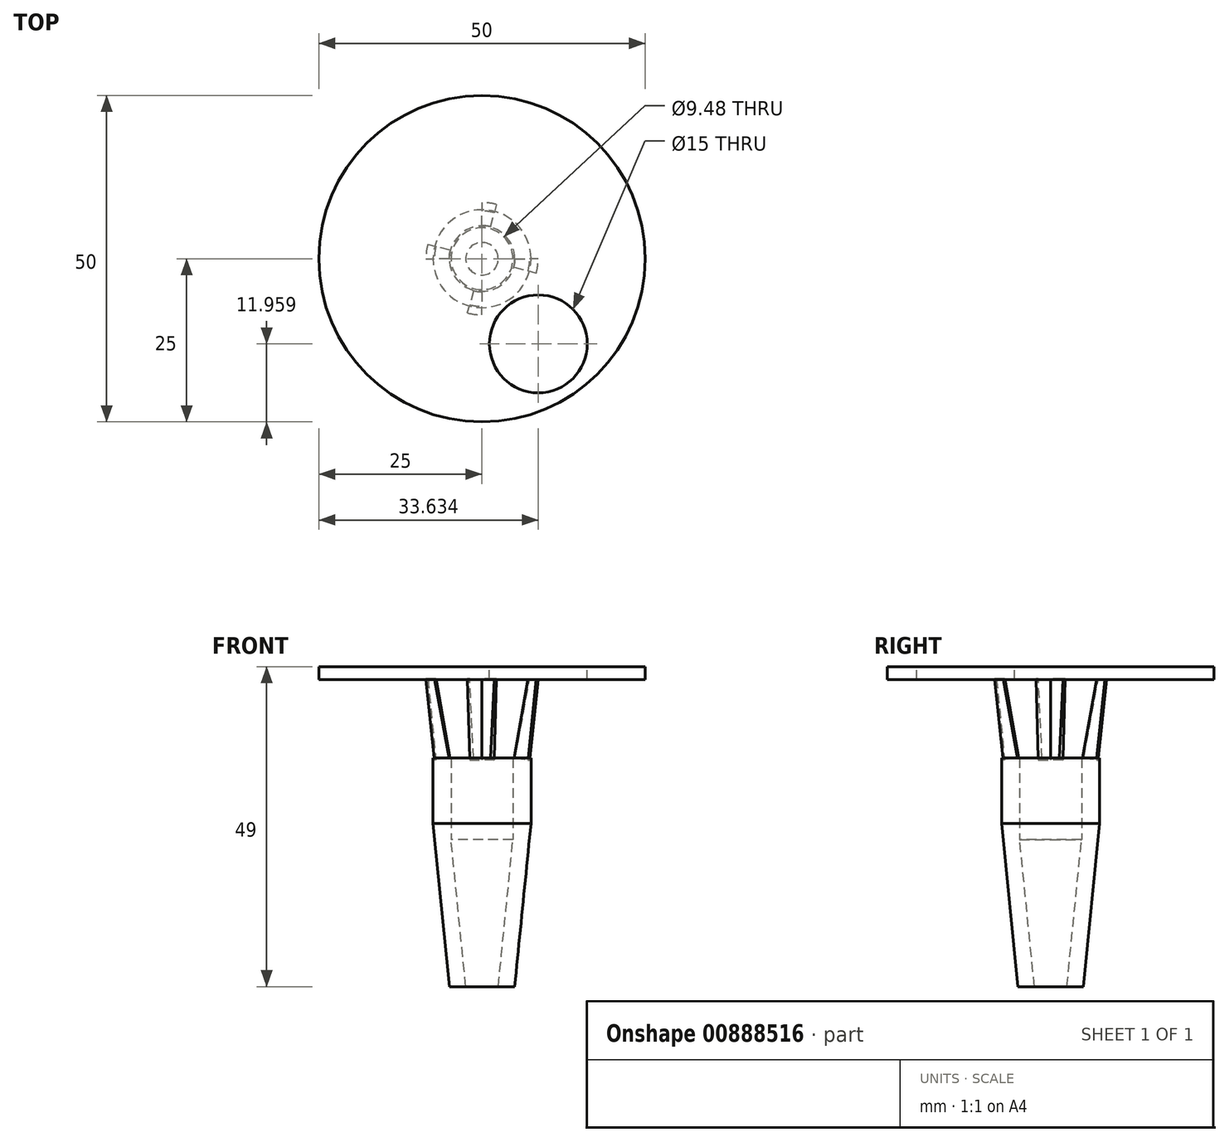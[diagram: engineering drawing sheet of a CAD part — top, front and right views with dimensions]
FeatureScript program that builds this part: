
annotation { "Feature Type Name" : "Feature", "Feature Type Description" : "" }
export const myFeature = defineFeature(function(context is Context, id is Id, definition is map)
    precondition{}
    {
        {
            var Q0;
            Q0=qCreatedBy(makeId("Top.planeOp"),FACE);
            var sketch = newSketch(context, id + "F0", { "sketchPlane" : qUnion([Q0])});
            skCircle(sketch, "E0", {"center": v(0, 0) * mm, "radius": 5 * mm});
            skSolve(sketch);
        }
        {
            var Q0;
            Q0=qCreatedBy(makeId("Top.planeOp"),FACE);
            cPlane(context, id + "F1", {"entities" : qUnion([Q0]), "cplaneType" : CPlaneType.OFFSET, "offset" : 25 * mm, "width" : 150 * mm, "height" : 150 * mm});
        }
        {
            var Q0;
            Q0=qCreatedBy(id+"F1.planeOp",FACE);
            var sketch = newSketch(context, id + "F2", { "sketchPlane" : qUnion([Q0])});
            skCircle(sketch, "E1", {"center": v(0, 0) * mm, "radius": 7.5 * mm});
            skSolve(sketch);
        }
        {
            var Q0;
            Q0=makeQuery(id+"F0.imprint","IMPRINT",FACE,{"disambiguationData":[TD([[makeQuery(id+"F0.imprint","IMPRINT",EDGE,{"derivedFrom":sQuery(id+"F0.wireOp",EDGE,"E0")}),1.0]])]});
            var Q1;
            Q1=makeQuery(id+"F2.imprint","IMPRINT",FACE,{"disambiguationData":[TD([[makeQuery(id+"F2.imprint","IMPRINT",EDGE,{"derivedFrom":sQuery(id+"F2.wireOp",EDGE,"E1")}),1.0]])]});
            loft(context, id + "F3", {"sheetProfilesArray" : [{ "sheetProfileEntities" : qUnion([Q0]) }, { "sheetProfileEntities" : qUnion([Q1]) }]});
        }
        {
            var Q0;
            Q0=makeQuery(id+"F3.opLoft","CAP_FACE",FACE,{"disambiguationData":[OSD([makeQuery(id+"F0.imprint","IMPRINT",FACE,{"disambiguationData":[TD([[makeQuery(id+"F0.imprint","IMPRINT",EDGE,{"derivedFrom":sQuery(id+"F0.wireOp",EDGE,"E0")}),1.0]])]})])],"isStart":true});
            var Q1;
            Q1=makeQuery(id+"F3.opLoft","SWEPT_BODY",BODY,{"disambiguationData":[OSD([makeQuery(id+"F0.imprint","IMPRINT",FACE,{"disambiguationData":[TD([[makeQuery(id+"F0.imprint","IMPRINT",EDGE,{"derivedFrom":sQuery(id+"F0.wireOp",EDGE,"E0")}),1.0]])]}),makeQuery(id+"F2.imprint","IMPRINT",FACE,{"disambiguationData":[TD([[makeQuery(id+"F2.imprint","IMPRINT",EDGE,{"derivedFrom":sQuery(id+"F2.wireOp",EDGE,"E1")}),1.0]])]})])]});
            shell(context, id + "F4", {"entities" : qUnion([Q0]), "parts" : qUnion([Q1]), "thickness" : 2.5 * mm});
        }
        {
            var Q0;
            Q0=makeQuery(id+"F4.opShell","OFFSET_FACE",FACE,{"disambiguationData":[OSD([makeQuery(id+"F2.imprint","IMPRINT",FACE,{"disambiguationData":[TD([[makeQuery(id+"F2.imprint","IMPRINT",EDGE,{"derivedFrom":sQuery(id+"F2.wireOp",EDGE,"E1")}),1.0]])]})])]});
            extrude(context, id + "F5", {"entities" : qUnion([Q0]), "operationType" : NewBodyOperationType.REMOVE, "oppositeDirection" : true, "depth" : 25 * mm, "offsetDistance" : 25 * mm});
        }
        {
            var Q0;
            Q0=makeQuery(id+"F3.opLoft","CAP_FACE",FACE,{"disambiguationData":[OSD([makeQuery(id+"F2.imprint","IMPRINT",FACE,{"disambiguationData":[TD([[makeQuery(id+"F2.imprint","IMPRINT",EDGE,{"derivedFrom":sQuery(id+"F2.wireOp",EDGE,"E1")}),1.0]])]})])],"isStart":true});
            extrude(context, id + "F6", {"entities" : qUnion([Q0]), "operationType" : NewBodyOperationType.ADD, "depth" : 10 * mm, "offsetDistance" : 25 * mm});
        }
        {
            var Q0;
            Q0=makeQuery(id+"F6.opExtrude","CAP_FACE",FACE,{"disambiguationData":[OSD([makeQuery(id+"F2.imprint","IMPRINT",FACE,{"disambiguationData":[TD([[makeQuery(id+"F2.imprint","IMPRINT",EDGE,{"derivedFrom":sQuery(id+"F2.wireOp",EDGE,"E1")}),1.0]])]})])],"isStart":false});
            cPlane(context, id + "F7", {"entities" : qUnion([Q0]), "cplaneType" : CPlaneType.OFFSET, "offset" : 12 * mm, "width" : 150 * mm, "height" : 150 * mm});
        }
        {
            var Q0;
            Q0=qCreatedBy(id+"F7.planeOp",FACE);
            var sketch = newSketch(context, id + "F8", { "sketchPlane" : qUnion([Q0])});
            skCircle(sketch, "E2", {"center": v(0, 0) * mm, "radius": 25 * mm});
            skSolve(sketch);
        }
        {
            var Q0;
            Q0 = qSketchRegion(id + "F8", true);
            extrude(context, id + "F9", {"entities" : qUnion([Q0]), "depth" : 2 * mm, "offsetDistance" : 25 * mm});
        }
        {
            var Q0;
            Q0=qCreatedBy(makeId("Front.planeOp"),FACE);
            var sketch = newSketch(context, id + "F10", { "sketchPlane" : qUnion([Q0])});
            skLineSegment(sketch, "E3", {"start": v(5.07, 35.02) * mm, "end": v(7.3, 47.18) * mm});
            skLineSegment(sketch, "E4", {"start": v(7.3, 47.18) * mm, "end": v(8.6, 47.18) * mm});
            skLineSegment(sketch, "E5", {"start": v(8.6, 47.18) * mm, "end": v(7.3, 34.74) * mm});
            skLineSegment(sketch, "E6", {"start": v(5.07, 35.02) * mm, "end": v(7.3, 34.74) * mm});
            skLineSegment(sketch, "E7", {"start": v(0, 48.1) * mm, "end": v(0, 33.44) * mm, "construction": true});
            skSolve(sketch);
        }
        {
            var Q0;
            Q0=makeQuery(id+"F10.imprint","IMPRINT",FACE,{"disambiguationData":[TD([[makeQuery(id+"F10.imprint","IMPRINT",EDGE,{"derivedFrom":sQuery(id+"F10.wireOp",EDGE,"E3")}),-1.0]])]});
            var Q1;
            Q1=sQuery(id+"F10.wireOp",EDGE,"E7");
            revolve(context, id + "F11", {"surfaceOperationType" : NewSurfaceOperationType.NEW, "entities" : qUnion([Q0]), "axis" : qUnion([Q1]), "revolveType" : RevolveType.ONE_DIRECTION, "angle" : 15 * degree});
        }
        {
            var Q0;
            Q0=makeQuery(id+"F11.opRevolve","SWEPT_BODY",BODY,{"disambiguationData":[OSD([sQuery(id+"F10.wireOp",EDGE,"E3"),sQuery(id+"F10.wireOp",EDGE,"E4"),sQuery(id+"F10.wireOp",EDGE,"E5"),sQuery(id+"F10.wireOp",EDGE,"E6")])]});
            var Q1;
            Q1=sQuery(id+"F10.wireOp",EDGE,"E7");
            circularPattern(context, id + "F12", {"entities" : qUnion([Q0]), "axis" : qUnion([Q1]), "angle" : 360 * degree, "instanceCount" : 4, "equalSpace" : true});
        }
        {
            var Q0;
            Q0=makeQuery(id+"F9.opExtrude","CAP_FACE",FACE,{"disambiguationData":[OSD([sQuery(id+"F8.wireOp",EDGE,"E2")])],"isStart":false});
            var sketch = newSketch(context, id + "F13", { "sketchPlane" : qUnion([Q0])});
            skCircle(sketch, "E8", {"center": v(8.63, -13.04) * mm, "radius": 7.5 * mm});
            skSolve(sketch);
        }
        {
            var Q0;
            Q0=makeQuery(id+"F13.imprint","IMPRINT",FACE,{"disambiguationData":[TD([[makeQuery(id+"F13.imprint","IMPRINT",EDGE,{"derivedFrom":sQuery(id+"F13.wireOp",EDGE,"E8")}),1.0]])]});
            extrude(context, id + "F14", {"entities" : qUnion([Q0]), "operationType" : NewBodyOperationType.REMOVE, "oppositeDirection" : true, "depth" : 25 * mm, "offsetDistance" : 25 * mm});
        }
    });
